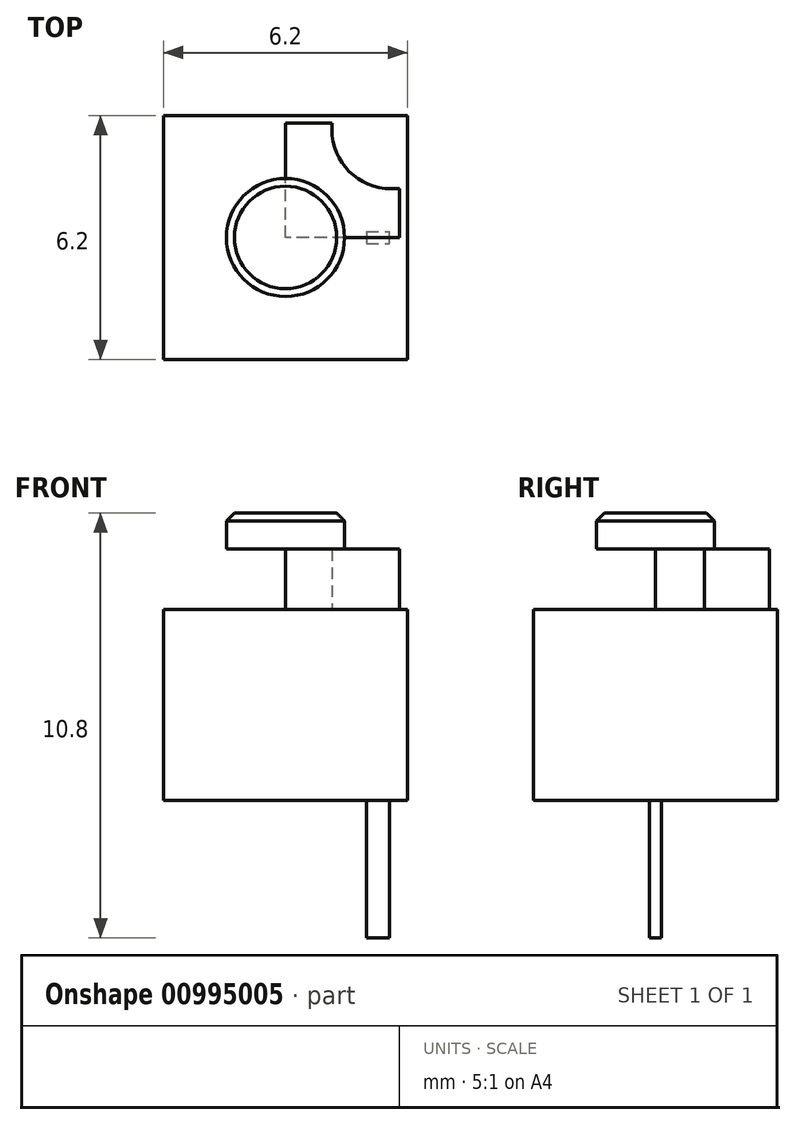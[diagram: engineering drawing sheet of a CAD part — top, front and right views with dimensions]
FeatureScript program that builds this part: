
annotation { "Feature Type Name" : "Feature", "Feature Type Description" : "" }
export const myFeature = defineFeature(function(context is Context, id is Id, definition is map)
    precondition{}
    {
        {
            var Q0;
            Q0=qCreatedBy(makeId("Top.planeOp"),FACE);
            var sketch = newSketch(context, id + "F0", { "sketchPlane" : qUnion([Q0])});
            skLineSegment(sketch, "E0.bottom", {"start": v(3.1, 3.1) * mm, "end": v(-3.1, 3.1) * mm});
            skLineSegment(sketch, "E0.top", {"start": v(3.1, -3.1) * mm, "end": v(-3.1, -3.1) * mm});
            skLineSegment(sketch, "E0.left", {"start": v(3.1, 3.1) * mm, "end": v(3.1, -3.1) * mm});
            skLineSegment(sketch, "E0.right", {"start": v(-3.1, 3.1) * mm, "end": v(-3.1, -3.1) * mm});
            skPoint(sketch, "E0.middle", {"position": v(0, 0) * mm});
            skSolve(sketch);
        }
        {
            var Q0;
            Q0=qSketchRegion(id+"F0",true);
            extrude(context, id + "F1", {"entities" : qUnion([Q0]), "depth" : 4.85 * mm, "offsetDistance" : 25 * mm});
        }
        {
            var Q0;
            Q0=makeQuery(id+"F1.opExtrude","CAP_FACE",FACE,{"disambiguationData":[OSD([sQuery(id+"F0.wireOp",EDGE,"E0.bottom"),sQuery(id+"F0.wireOp",EDGE,"E0.top"),sQuery(id+"F0.wireOp",EDGE,"E0.left"),sQuery(id+"F0.wireOp",EDGE,"E0.right")])],"isStart":false});
            var sketch = newSketch(context, id + "F2", { "sketchPlane" : qUnion([Q0])});
            skLineSegment(sketch, "E1", {"start": v(0, 2.9) * mm, "end": v(1.18, 2.9) * mm});
            skLineSegment(sketch, "E2", {"start": v(2.9, 1.24) * mm, "end": v(2.9, 0) * mm});
            skLineSegment(sketch, "E3", {"start": v(2.9, 0) * mm, "end": v(0, 0) * mm});
            skLineSegment(sketch, "E4", {"start": v(0, 0) * mm, "end": v(0, 2.9) * mm});
            skLineSegment(sketch, "E5", {"start": v(1.18, 2.9) * mm, "end": v(1.18, 2.74) * mm});
            skLineSegment(sketch, "E6", {"start": v(2.9, 1.24) * mm, "end": v(2.68, 1.24) * mm});
            skPoint(sketch, "E7.visualSharp", {"position": v(1.18, 1.24) * mm});
            skArc(sketch, "E7.filletArc", {"start": v(1.18, 2.74) * mm, "mid": v(1.62, 1.68) * mm, "end": v(2.68, 1.24) * mm});
            skSolve(sketch);
        }
        {
            var Q0;
            Q0=qSketchRegion(id+"F2",true);
            extrude(context, id + "F3", {"entities" : qUnion([Q0]), "operationType" : NewBodyOperationType.ADD, "depth" : (6.38 - 4.85) * mm, "offsetDistance" : 25 * mm});
        }
        {
            var Q0;
            Q0=qCreatedBy(makeId("Front.planeOp"),FACE);
            var sketch = newSketch(context, id + "F4", { "sketchPlane" : qUnion([Q0])});
            skLineSegment(sketch, "E8", {"start": v(0, 5.34) * mm, "end": v(0, 7.15) * mm});
            skSolve(sketch);
        }
        {
            var Q0;
            {var subQ0=sQuery(id+"F2.wireOp",EDGE,"E7.filletArc");var subQ1=sQuery(id+"F2.wireOp",EDGE,"E6");var subQ2=sQuery(id+"F2.wireOp",EDGE,"E5");var subQ3=sQuery(id+"F2.wireOp",EDGE,"E4");var subQ4=sQuery(id+"F2.wireOp",EDGE,"E3");var subQ5=sQuery(id+"F2.wireOp",EDGE,"E2");var subQ6=sQuery(id+"F2.wireOp",EDGE,"E1");Q0=makeQuery(id+"FWAw8H5S5yVXPhM_1.3.F3.boolean.opBoolean","MERGE",FACE,{"derivedFrom":[makeQuery(id+"FWAw8H5S5yVXPhM_1.2.F3.boolean.opBoolean","MERGE",FACE,{"derivedFrom":[makeQuery(id+"FWAw8H5S5yVXPhM_1.1.F3.boolean.opBoolean","MERGE",FACE,{"derivedFrom":[makeQuery(id+"F3.opExtrude","CAP_FACE",FACE,{"disambiguationData":[OSD([subQ6,subQ5,subQ4,subQ3,subQ2,subQ1,subQ0])],"isStart":false}),makeQuery(id+"FWAw8H5S5yVXPhM_1.1.F3.opExtrude","CAP_FACE",FACE,{"disambiguationData":[OSD([subQ6,subQ5,subQ4,subQ3,subQ2,subQ1,subQ0])],"isStart":false})]}),makeQuery(id+"FWAw8H5S5yVXPhM_1.2.F3.opExtrude","CAP_FACE",FACE,{"disambiguationData":[OSD([subQ6,subQ5,subQ4,subQ3,subQ2,subQ1,subQ0])],"isStart":false})]}),makeQuery(id+"FWAw8H5S5yVXPhM_1.3.F3.opExtrude","CAP_FACE",FACE,{"disambiguationData":[OSD([subQ6,subQ5,subQ4,subQ3,subQ2,subQ1,subQ0])],"isStart":false})]});}
            var sketch = newSketch(context, id + "F5", { "sketchPlane" : qUnion([Q0])});
            skCircle(sketch, "E9", {"center": v(0, 0) * mm, "radius": 1.5 * mm});
            skSolve(sketch);
        }
        {
            var Q0;
            Q0=qSketchRegion(id+"F5",true);
            extrude(context, id + "F6", {"entities" : qUnion([Q0]), "operationType" : NewBodyOperationType.ADD, "depth" : (7.3 - 6.38) * mm, "offsetDistance" : 25 * mm});
        }
        {
            var Q0;
            Q0=makeQuery(id+"F6.opExtrude","CAP_EDGE",EDGE,{"disambiguationData":[OSD([sQuery(id+"F5.wireOp",EDGE,"E9")])],"isStart":false});
            chamfer(context, id + "F7", {"entities" : qUnion([Q0]), "width" : 0.2 * mm, "tangentPropagation" : true});
        }
        {
            var Q0;
            Q0=qCreatedBy(makeId("Front.planeOp"),FACE);
            var sketch = newSketch(context, id + "F8", { "sketchPlane" : qUnion([Q0])});
            skLineSegment(sketch, "E10", {"start": v(2.64, 0.4) * mm, "end": v(2.64, -3.5) * mm});
            skLineSegment(sketch, "E11", {"start": v(2.64, -3.5) * mm, "end": v(2.06, -3.5) * mm});
            skLineSegment(sketch, "E12", {"start": v(2.06, -3.5) * mm, "end": v(2.06, 0.4) * mm});
            skLineSegment(sketch, "E13", {"start": v(2.06, 0.4) * mm, "end": v(2.64, 0.4) * mm});
            skPoint(sketch, "E14", {"position": v(2.35, 0.4) * mm});
            skSolve(sketch);
        }
        {
            var Q0;
            Q0=qSketchRegion(id+"F8",true);
            extrude(context, id + "F9", {"entities" : qUnion([Q0]), "operationType" : NewBodyOperationType.ADD, "endBound" : BoundingType.SYMMETRIC, "depth" : 0.3 * mm, "offsetDistance" : 25 * mm});
        }
    });
